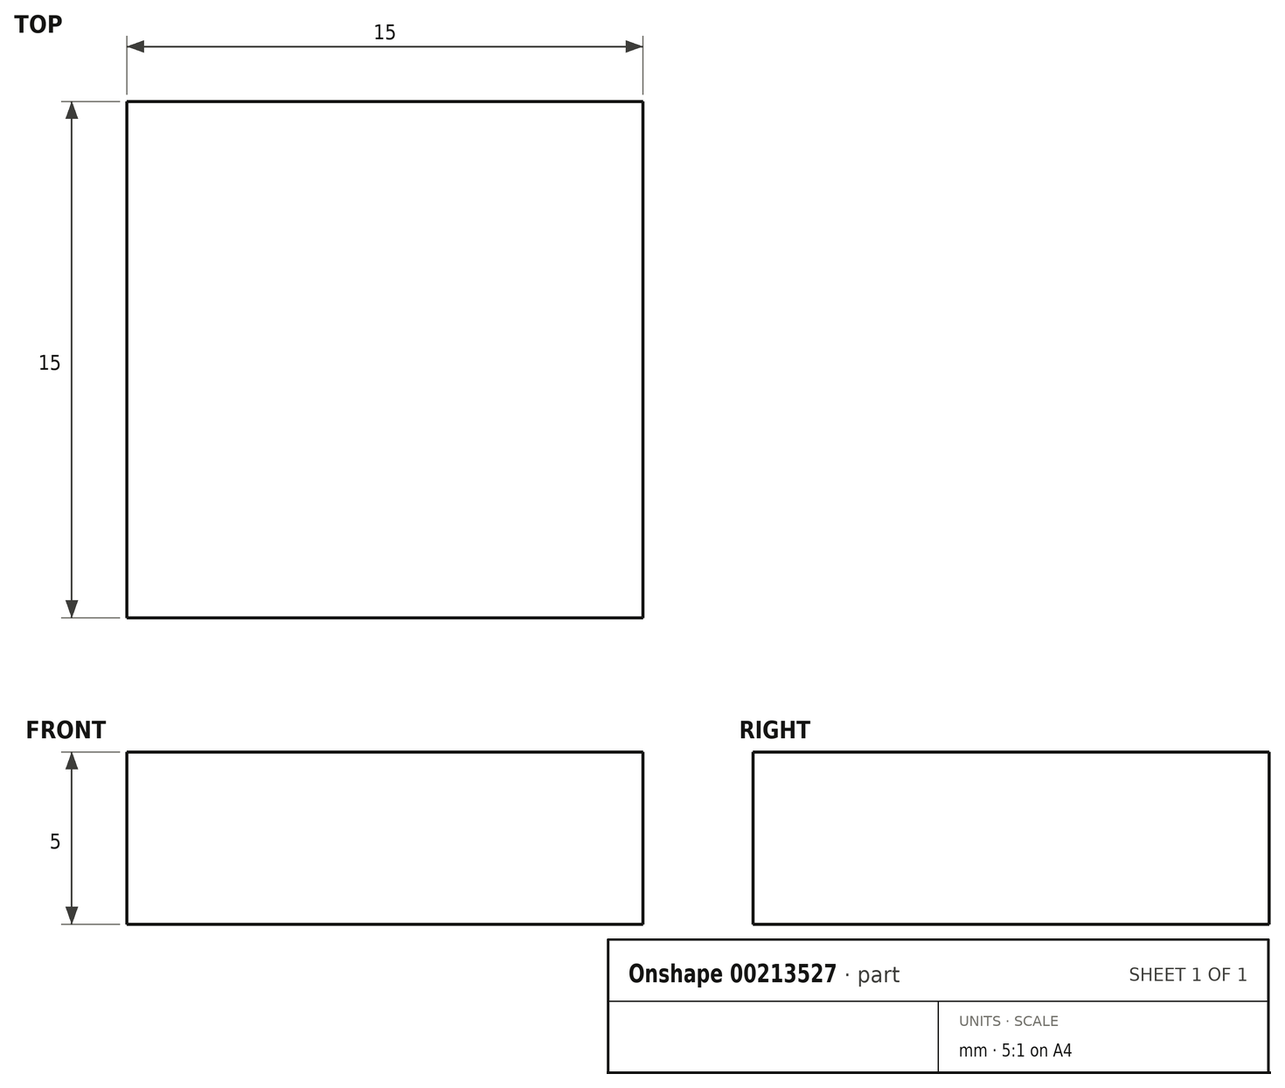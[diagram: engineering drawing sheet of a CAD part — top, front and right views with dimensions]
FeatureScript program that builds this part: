
annotation { "Feature Type Name" : "Feature", "Feature Type Description" : "" }
export const myFeature = defineFeature(function(context is Context, id is Id, definition is map)
    precondition{}
    {
        {
            var Q0;
            Q0=qCreatedBy(makeId("Top.planeOp"),FACE);
            var sketch = newSketch(context, id + "F0", { "sketchPlane" : qUnion([Q0])});
            skLineSegment(sketch, "E0.bottom", {"start": v(7.5, 7.5) * mm, "end": v(-7.5, 7.5) * mm});
            skLineSegment(sketch, "E0.top", {"start": v(7.5, -7.5) * mm, "end": v(-7.5, -7.5) * mm});
            skLineSegment(sketch, "E0.left", {"start": v(7.5, 7.5) * mm, "end": v(7.5, -7.5) * mm});
            skLineSegment(sketch, "E0.right", {"start": v(-7.5, 7.5) * mm, "end": v(-7.5, -7.5) * mm});
            skPoint(sketch, "E0.middle", {"position": v(0, 0) * mm});
            skSolve(sketch);
        }
        {
            var Q0;
            Q0 = qSketchRegion(id + "F0", true);
            extrude(context, id + "F1", {"entities" : qUnion([Q0]), "depth" : 5 * mm});
        }
    });
